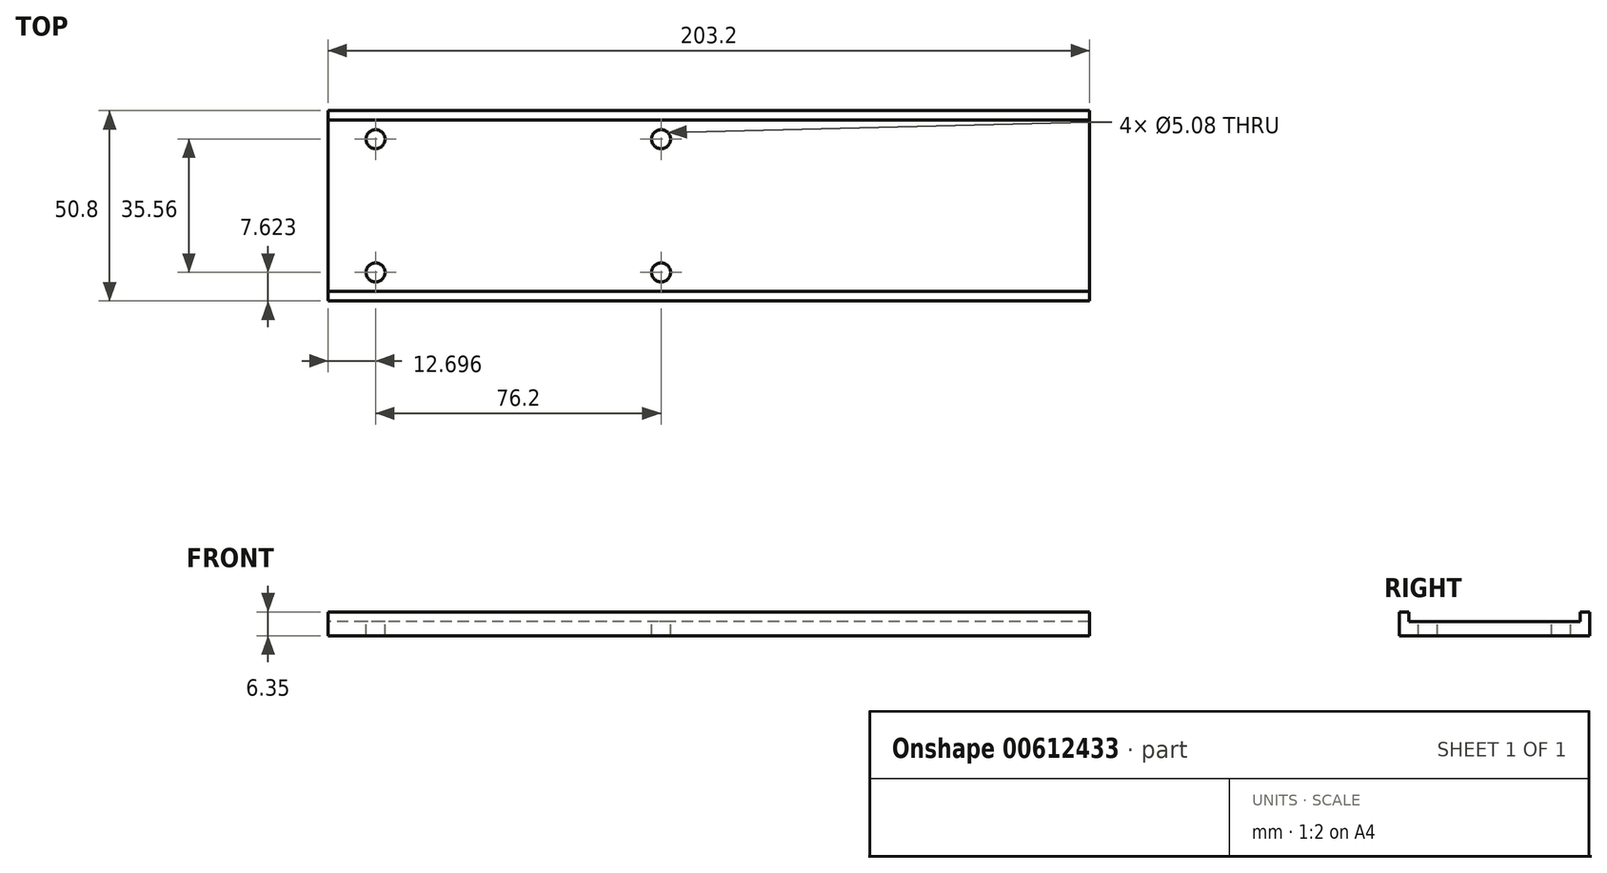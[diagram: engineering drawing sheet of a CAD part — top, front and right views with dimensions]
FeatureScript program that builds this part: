
annotation { "Feature Type Name" : "Feature", "Feature Type Description" : "" }
export const myFeature = defineFeature(function(context is Context, id is Id, definition is map)
    precondition{}
    {
        {
            var Q0;
            Q0=qCreatedBy(makeId("Top.planeOp"),FACE);
            var sketch = newSketch(context, id + "F0", { "sketchPlane" : qUnion([Q0])});
            skLineSegment(sketch, "E0.bottom", {"start": v(-99.83, 14.75) * mm, "end": v(103.37, 14.75) * mm});
            skLineSegment(sketch, "E0.top", {"start": v(-99.83, -36.05) * mm, "end": v(103.37, -36.05) * mm});
            skLineSegment(sketch, "E0.left", {"start": v(-99.83, 14.75) * mm, "end": v(-99.83, -36.05) * mm});
            skLineSegment(sketch, "E0.right", {"start": v(103.37, 14.75) * mm, "end": v(103.37, -36.05) * mm});
            skSolve(sketch);
        }
        {
            var Q0;
            Q0 = qSketchRegion(id + "F0", true);
            extrude(context, id + "F1", {"entities" : qUnion([Q0]), "depth" : 3.8 * mm, "offsetDistance" : 25.4 * mm});
        }
        {
            var Q0;
            Q0=makeQuery(id+"F1.opExtrude","CAP_FACE",FACE,{"disambiguationData":[OSD([sQuery(id+"F0.wireOp",EDGE,"E0.bottom"),sQuery(id+"F0.wireOp",EDGE,"E0.top"),sQuery(id+"F0.wireOp",EDGE,"E0.left"),sQuery(id+"F0.wireOp",EDGE,"E0.right")])],"isStart":false});
            var sketch = newSketch(context, id + "F2", { "sketchPlane" : qUnion([Q0])});
            skLineSegment(sketch, "E1.bottom", {"start": v(-99.83, 14.75) * mm, "end": v(103.37, 14.75) * mm});
            skLineSegment(sketch, "E1.top", {"start": v(-99.83, 12.21) * mm, "end": v(103.37, 12.21) * mm});
            skLineSegment(sketch, "E1.left", {"start": v(-99.83, 14.75) * mm, "end": v(-99.83, 12.21) * mm});
            skLineSegment(sketch, "E1.right", {"start": v(103.37, 14.75) * mm, "end": v(103.37, 12.21) * mm});
            skLineSegment(sketch, "E2.bottom", {"start": v(103.37, -36.05) * mm, "end": v(-99.83, -36.05) * mm});
            skLineSegment(sketch, "E2.top", {"start": v(103.37, -33.5) * mm, "end": v(-99.83, -33.5) * mm});
            skLineSegment(sketch, "E2.left", {"start": v(103.37, -36.05) * mm, "end": v(103.37, -33.5) * mm});
            skLineSegment(sketch, "E2.right", {"start": v(-99.83, -36.05) * mm, "end": v(-99.83, -33.5) * mm});
            skSolve(sketch);
        }
        {
            var Q0;
            Q0 = qSketchRegion(id + "F2", true);
            extrude(context, id + "F3", {"entities" : qUnion([Q0]), "operationType" : NewBodyOperationType.ADD, "depth" : 2.54 * mm, "offsetDistance" : 25.4 * mm});
        }
        {
            var Q0;
            Q0=makeQuery(id+"F1.opExtrude","CAP_FACE",FACE,{"disambiguationData":[OSD([sQuery(id+"F0.wireOp",EDGE,"E0.bottom"),sQuery(id+"F0.wireOp",EDGE,"E0.top"),sQuery(id+"F0.wireOp",EDGE,"E0.left"),sQuery(id+"F0.wireOp",EDGE,"E0.right")])],"isStart":false});
            var sketch = newSketch(context, id + "F4", { "sketchPlane" : qUnion([Q0])});
            skCircle(sketch, "E3", {"center": v(-87.13, 7.13) * mm, "radius": 2.54 * mm});
            skCircle(sketch, "E4", {"center": v(-87.13, -28.43) * mm, "radius": 2.54 * mm});
            skCircle(sketch, "E5", {"center": v(-10.93, 7.13) * mm, "radius": 2.54 * mm});
            skCircle(sketch, "E6", {"center": v(-10.93, -28.43) * mm, "radius": 2.54 * mm});
            skSolve(sketch);
        }
        {
            var Q0;
            Q0 = qSketchRegion(id + "F4", true);
            extrude(context, id + "F5", {"entities" : qUnion([Q0]), "operationType" : NewBodyOperationType.REMOVE, "oppositeDirection" : true, "depth" : 3.8 * mm, "offsetDistance" : 25.4 * mm});
        }
    });
